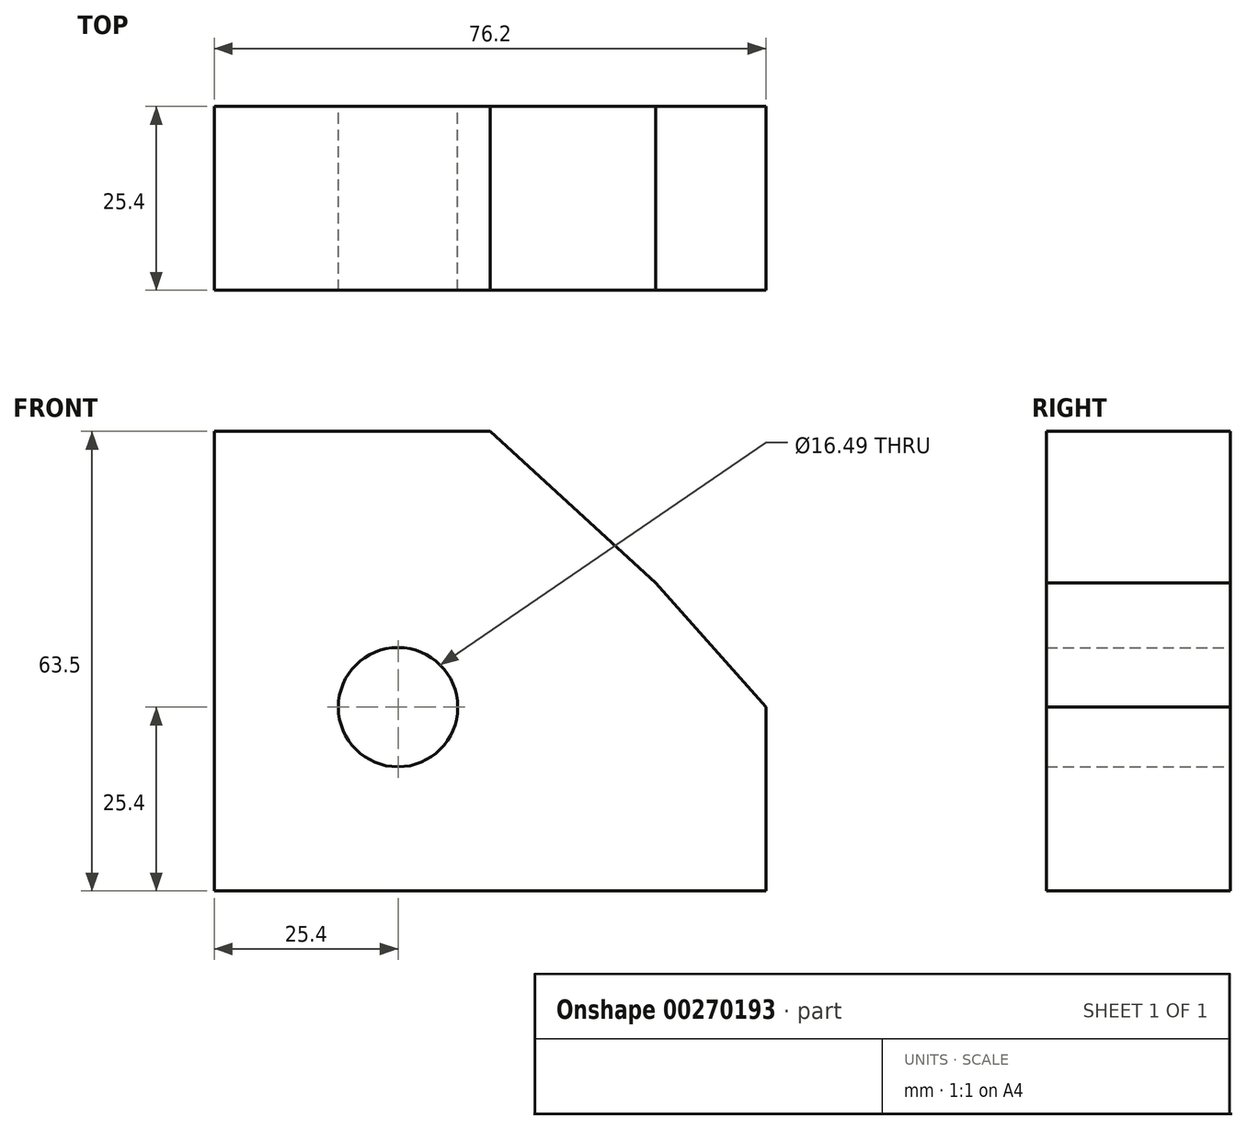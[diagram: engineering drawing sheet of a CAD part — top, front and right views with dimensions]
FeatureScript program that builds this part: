
annotation { "Feature Type Name" : "Feature", "Feature Type Description" : "" }
export const myFeature = defineFeature(function(context is Context, id is Id, definition is map)
    precondition{}
    {
        {
            var Q0;
            Q0=qCreatedBy(makeId("Front.planeOp"),FACE);
            var sketch = newSketch(context, id + "F0", { "sketchPlane" : qUnion([Q0])});
            skLineSegment(sketch, "E0", {"start": v(0, 0) * mm, "end": v(76.2, 0) * mm});
            skLineSegment(sketch, "E1", {"start": v(76.2, 0) * mm, "end": v(76.2, 25.4) * mm});
            skLineSegment(sketch, "E2", {"start": v(60.96, 42.55) * mm, "end": v(38.1, 63.5) * mm});
            skLineSegment(sketch, "E3", {"start": v(38.1, 63.5) * mm, "end": v(0, 63.5) * mm});
            skLineSegment(sketch, "E4", {"start": v(0, 63.5) * mm, "end": v(0, 0) * mm});
            skCircle(sketch, "E5", {"center": v(25.4, 25.4) * mm, "radius": 8.24 * mm});
            skLineSegment(sketch, "E6", {"start": v(60.96, 42.55) * mm, "end": v(76.2, 25.4) * mm});
            skSolve(sketch);
        }
        {
            var Q0;
            Q0=qSketchRegion(id+"F0",true);
            extrude(context, id + "F1", {"entities" : qUnion([Q0]), "depth" : 25.4 * mm});
        }
    });
